MODEL slx_9b403d1e33a8
CONFIG AbsTol = auto
CONFIG EnableMultiTasking = off
CONFIG FixedStep = auto
CONFIG MaxStep = auto
CONFIG MinStep = auto
CONFIG RelTol = 1e-3
CONFIG SampleTimeConstraint = Unconstrained
CONFIG Solver = VariableStepAuto
CONFIG SolverName = VariableStepAuto
CONFIG StartTime = 0.0
CONFIG StopTime = 10.0
BLOCK [SubSystem] CAD2_1
  Ports = [0, 0, 0, 0, 0, 1, 1]
  RequestExecContextInheritance = off
BLOCK [PMIOPort] CAD2_1/F
  Port = 2
  Side = Right
BLOCK [PMIOPort] CAD2_1/F1
  Side = Left
BLOCK [Reference] CAD2_1/ReferenceFrame  REF=sm_lib/Frames and
Transforms/Reference
Frame
  Ports = [0, 0, 0, 0, 0, 0, 1]
  SourceBlock = sm_lib/Frames and
Transforms/Reference
Frame
  SourceProductBaseCode = MS
  SourceType = Reference
Frame
BLOCK [Reference] CAD2_1/Solid  REF=sm_lib/Body Elements/File Solid
  Ports = [0, 0, 0, 0, 0, 0, 1]
  SourceBlock = sm_lib/Body Elements/File Solid
  SourceProductBaseCode = MS
  SourceType = File Solid
BLOCK [Reference] CAD2_1/Transform  REF=sm_lib/Frames and
Transforms/Rigid
Transform
  Ports = [0, 0, 0, 0, 0, 1, 1]
  SourceBlock = sm_lib/Frames and
Transforms/Rigid
Transform
  SourceProductBaseCode = MS
  SourceType = Rigid
Transform
BLOCK [SubSystem] CAD2_2
  Ports = [0, 0, 0, 0, 0, 1, 1]
  RequestExecContextInheritance = off
BLOCK [PMIOPort] CAD2_2/F
  Side = Left
BLOCK [PMIOPort] CAD2_2/F1
  Port = 2
  Side = Right
BLOCK [Reference] CAD2_2/ReferenceFrame  REF=sm_lib/Frames and
Transforms/Reference
Frame
  Ports = [0, 0, 0, 0, 0, 0, 1]
  SourceBlock = sm_lib/Frames and
Transforms/Reference
Frame
  SourceProductBaseCode = MS
  SourceType = Reference
Frame
BLOCK [Reference] CAD2_2/Solid  REF=sm_lib/Body Elements/File Solid
  Ports = [0, 0, 0, 0, 0, 0, 1]
  SourceBlock = sm_lib/Body Elements/File Solid
  SourceProductBaseCode = MS
  SourceType = File Solid
BLOCK [Reference] CAD2_2/Transform  REF=sm_lib/Frames and
Transforms/Rigid
Transform
  Ports = [0, 0, 0, 0, 0, 1, 1]
  SourceBlock = sm_lib/Frames and
Transforms/Rigid
Transform
  SourceProductBaseCode = MS
  SourceType = Rigid
Transform
BLOCK [Reference] CAD2_2/Transform1  REF=sm_lib/Frames and
Transforms/Rigid
Transform
  Ports = [0, 0, 0, 0, 0, 1, 1]
  SourceBlock = sm_lib/Frames and
Transforms/Rigid
Transform
  SourceProductBaseCode = MS
  SourceType = Rigid
Transform
BLOCK [SubSystem] CAD2_3
  Ports = [0, 0, 0, 0, 0, 1, 1]
  RequestExecContextInheritance = off
BLOCK [PMIOPort] CAD2_3/F
  Port = 2
  Side = Right
BLOCK [PMIOPort] CAD2_3/F1
  Side = Left
BLOCK [Reference] CAD2_3/ReferenceFrame  REF=sm_lib/Frames and
Transforms/Reference
Frame
  Ports = [0, 0, 0, 0, 0, 0, 1]
  SourceBlock = sm_lib/Frames and
Transforms/Reference
Frame
  SourceProductBaseCode = MS
  SourceType = Reference
Frame
BLOCK [Reference] CAD2_3/Solid  REF=sm_lib/Body Elements/File Solid
  Ports = [0, 0, 0, 0, 0, 0, 1]
  SourceBlock = sm_lib/Body Elements/File Solid
  SourceProductBaseCode = MS
  SourceType = File Solid
BLOCK [Reference] CAD2_3/Transform  REF=sm_lib/Frames and
Transforms/Rigid
Transform
  Ports = [0, 0, 0, 0, 0, 1, 1]
  SourceBlock = sm_lib/Frames and
Transforms/Rigid
Transform
  SourceProductBaseCode = MS
  SourceType = Rigid
Transform
BLOCK [Reference] CAD2_3/Transform1  REF=sm_lib/Frames and
Transforms/Rigid
Transform
  Ports = [0, 0, 0, 0, 0, 1, 1]
  SourceBlock = sm_lib/Frames and
Transforms/Rigid
Transform
  SourceProductBaseCode = MS
  SourceType = Rigid
Transform
BLOCK [SubSystem] CAD_1
  Ports = [0, 0, 0, 0, 0, 2]
  RequestExecContextInheritance = off
BLOCK [PMIOPort] CAD_1/F
  Port = 2
  Side = Left
BLOCK [PMIOPort] CAD_1/F1
  Side = Left
BLOCK [Reference] CAD_1/ReferenceFrame  REF=sm_lib/Frames and
Transforms/Reference
Frame
  Ports = [0, 0, 0, 0, 0, 0, 1]
  SourceBlock = sm_lib/Frames and
Transforms/Reference
Frame
  SourceProductBaseCode = MS
  SourceType = Reference
Frame
BLOCK [Reference] CAD_1/Solid  REF=sm_lib/Body Elements/File Solid
  Ports = [0, 0, 0, 0, 0, 0, 1]
  SourceBlock = sm_lib/Body Elements/File Solid
  SourceProductBaseCode = MS
  SourceType = File Solid
BLOCK [Reference] CAD_1/Transform  REF=sm_lib/Frames and
Transforms/Rigid
Transform
  Ports = [0, 0, 0, 0, 0, 1, 1]
  SourceBlock = sm_lib/Frames and
Transforms/Rigid
Transform
  SourceProductBaseCode = MS
  SourceType = Rigid
Transform
BLOCK [Constant] Constant
  Value = 50
BLOCK [Reference] MechanismConfiguration  REF=sm_lib/Utilities/Mechanism
Configuration
  Ports = [0, 0, 0, 0, 0, 0, 1]
  SourceBlock = sm_lib/Utilities/Mechanism
Configuration
  SourceProductBaseCode = MS
  SourceType = Mechanism
Configuration
BLOCK [Reference] Prismatic  REF=sm_lib/Joints/Prismatic
Joint
  Ports = [0, 0, 0, 0, 0, 2, 1]
  SourceBlock = sm_lib/Joints/Prismatic
Joint
  SourceProductBaseCode = MS
  SourceType = Prismatic
Joint
BLOCK [Reference] Prismatic1  REF=sm_lib/Joints/Prismatic
Joint
  Ports = [0, 0, 0, 0, 0, 1, 1]
  SourceBlock = sm_lib/Joints/Prismatic
Joint
  SourceProductBaseCode = MS
  SourceType = Prismatic
Joint
BLOCK [Reference] Prismatic2  REF=sm_lib/Joints/Prismatic
Joint
  Ports = [0, 0, 0, 0, 0, 2, 1]
  SourceBlock = sm_lib/Joints/Prismatic
Joint
  SourceProductBaseCode = MS
  SourceType = Prismatic
Joint
BLOCK [Reference] Prismatic3  REF=sm_lib/Joints/Prismatic
Joint
  Ports = [0, 0, 0, 0, 0, 2, 1]
  SourceBlock = sm_lib/Joints/Prismatic
Joint
  SourceProductBaseCode = MS
  SourceType = Prismatic
Joint
BLOCK [Reference] Revolute  REF=sm_lib/Joints/Revolute Joint
  Ports = [0, 0, 0, 0, 0, 2, 1]
  SourceBlock = sm_lib/Joints/Revolute Joint
  SourceProductBaseCode = MS
  SourceType = Revolute Joint
BLOCK [Reference] Simulink-PS Converter1  REF=nesl_utility/Simulink-PS
Converter
  Ports = [1, 0, 0, 0, 0, 0, 1]
  SourceBlock = nesl_utility/Simulink-PS
Converter
  SourceProductBaseCode = SS
  SourceType = Simulink-PS
Converter
BLOCK [Reference] Simulink-PS Converter2  REF=nesl_utility/Simulink-PS
Converter
  Ports = [1, 0, 0, 0, 0, 0, 1]
  SourceBlock = nesl_utility/Simulink-PS
Converter
  SourceProductBaseCode = SS
  SourceType = Simulink-PS
Converter
BLOCK [Reference] Simulink-PS Converter3  REF=nesl_utility/Simulink-PS
Converter
  Ports = [1, 0, 0, 0, 0, 0, 1]
  SourceBlock = nesl_utility/Simulink-PS
Converter
  SourceProductBaseCode = SS
  SourceType = Simulink-PS
Converter
BLOCK [Reference] Simulink-PS Converter4  REF=nesl_utility/Simulink-PS
Converter
  Ports = [1, 0, 0, 0, 0, 0, 1]
  SourceBlock = nesl_utility/Simulink-PS
Converter
  SourceProductBaseCode = SS
  SourceType = Simulink-PS
Converter
BLOCK [Sin] Sine Wave1
  Amplitude = 0.1/3
  Phase = 180
  Ports = [0, 1]
  SampleTime = 0
BLOCK [Sin] Sine Wave2
  Amplitude = 0.01
  Ports = [0, 1]
  SampleTime = 0
BLOCK [Sin] Sine Wave3
  Amplitude = 0.1/3
  Ports = [0, 1]
  SampleTime = 0
BLOCK [Reference] Solver Configuration  REF=nesl_utility/Solver
Configuration
  Ports = [0, 0, 0, 0, 0, 0, 1]
  SourceBlock = nesl_utility/Solver
Configuration
  SourceProductBaseCode = SS
  SourceType = Solver
Configuration
BLOCK [Reference] Transform  REF=sm_lib/Frames and
Transforms/Rigid
Transform
  Ports = [0, 0, 0, 0, 0, 1, 1]
  SourceBlock = sm_lib/Frames and
Transforms/Rigid
Transform
  SourceProductBaseCode = MS
  SourceType = Rigid
Transform
BLOCK [Reference] Transform1  REF=sm_lib/Frames and
Transforms/Rigid
Transform
  Ports = [0, 0, 0, 0, 0, 1, 1]
  SourceBlock = sm_lib/Frames and
Transforms/Rigid
Transform
  SourceProductBaseCode = MS
  SourceType = Rigid
Transform
BLOCK [Reference] World  REF=sm_lib/Frames and
Transforms/World Frame
  Ports = [0, 0, 0, 0, 0, 0, 1]
  SourceBlock = sm_lib/Frames and
Transforms/World Frame
  SourceProductBaseCode = MS
  SourceType = World Frame
BLOCK [SubSystem] spindle2_1
  Ports = [0, 0, 0, 0, 0, 1]
  RequestExecContextInheritance = off
BLOCK [PMIOPort] spindle2_1/F
  Side = Left
BLOCK [Reference] spindle2_1/ReferenceFrame  REF=sm_lib/Frames and
Transforms/Reference
Frame
  Ports = [0, 0, 0, 0, 0, 0, 1]
  SourceBlock = sm_lib/Frames and
Transforms/Reference
Frame
  SourceProductBaseCode = MS
  SourceType = Reference
Frame
BLOCK [Reference] spindle2_1/Solid  REF=sm_lib/Body Elements/File Solid
  Ports = [0, 0, 0, 0, 0, 0, 1]
  SourceBlock = sm_lib/Body Elements/File Solid
  SourceProductBaseCode = MS
  SourceType = File Solid
BLOCK [Reference] spindle2_1/Transform  REF=sm_lib/Frames and
Transforms/Rigid
Transform
  Ports = [0, 0, 0, 0, 0, 1, 1]
  SourceBlock = sm_lib/Frames and
Transforms/Rigid
Transform
  SourceProductBaseCode = MS
  SourceType = Rigid
Transform
BLOCK [SubSystem] spindle_1
  Ports = [0, 0, 0, 0, 0, 1, 1]
  RequestExecContextInheritance = off
BLOCK [PMIOPort] spindle_1/F
  Port = 2
  Side = Right
BLOCK [PMIOPort] spindle_1/F1
  Side = Left
BLOCK [Reference] spindle_1/ReferenceFrame  REF=sm_lib/Frames and
Transforms/Reference
Frame
  Ports = [0, 0, 0, 0, 0, 0, 1]
  SourceBlock = sm_lib/Frames and
Transforms/Reference
Frame
  SourceProductBaseCode = MS
  SourceType = Reference
Frame
BLOCK [Reference] spindle_1/Solid  REF=sm_lib/Body Elements/File Solid
  Ports = [0, 0, 0, 0, 0, 0, 1]
  SourceBlock = sm_lib/Body Elements/File Solid
  SourceProductBaseCode = MS
  SourceType = File Solid
BLOCK [Reference] spindle_1/Transform  REF=sm_lib/Frames and
Transforms/Rigid
Transform
  Ports = [0, 0, 0, 0, 0, 1, 1]
  SourceBlock = sm_lib/Frames and
Transforms/Rigid
Transform
  SourceProductBaseCode = MS
  SourceType = Rigid
Transform
BLOCK [Reference] spindle_1/Transform1  REF=sm_lib/Frames and
Transforms/Rigid
Transform
  Ports = [0, 0, 0, 0, 0, 1, 1]
  SourceBlock = sm_lib/Frames and
Transforms/Rigid
Transform
  SourceProductBaseCode = MS
  SourceType = Rigid
Transform
BLOCK [SubSystem] table_1
  Ports = [0, 0, 0, 0, 0, 1, 1]
  RequestExecContextInheritance = off
BLOCK [PMIOPort] table_1/F
  Side = Left
BLOCK [PMIOPort] table_1/F1
  Port = 2
  Side = Right
BLOCK [Reference] table_1/ReferenceFrame  REF=sm_lib/Frames and
Transforms/Reference
Frame
  Ports = [0, 0, 0, 0, 0, 0, 1]
  SourceBlock = sm_lib/Frames and
Transforms/Reference
Frame
  SourceProductBaseCode = MS
  SourceType = Reference
Frame
BLOCK [Reference] table_1/Solid  REF=sm_lib/Body Elements/File Solid
  Ports = [0, 0, 0, 0, 0, 0, 1]
  SourceBlock = sm_lib/Body Elements/File Solid
  SourceProductBaseCode = MS
  SourceType = File Solid
BLOCK [Reference] table_1/Transform  REF=sm_lib/Frames and
Transforms/Rigid
Transform
  Ports = [0, 0, 0, 0, 0, 1, 1]
  SourceBlock = sm_lib/Frames and
Transforms/Rigid
Transform
  SourceProductBaseCode = MS
  SourceType = Rigid
Transform
BLOCK [Reference] table_1/Transform1  REF=sm_lib/Frames and
Transforms/Rigid
Transform
  Ports = [0, 0, 0, 0, 0, 1, 1]
  SourceBlock = sm_lib/Frames and
Transforms/Rigid
Transform
  SourceProductBaseCode = MS
  SourceType = Rigid
Transform
BLOCK [SubSystem] table_2
  Ports = [0, 0, 0, 0, 0, 1]
  RequestExecContextInheritance = off
BLOCK [Reference] table_2/Brick Solid  REF=sm_lib/Body Elements/Brick Solid
  NameLocation = top
  Ports = [0, 0, 0, 0, 0, 1]
  SourceBlock = sm_lib/Body Elements/Brick Solid
  SourceProductBaseCode = MS
  SourceType = Brick Solid
BLOCK [PMIOPort] table_2/F
  Side = Left
BLOCK [Reference] table_2/ReferenceFrame  REF=sm_lib/Frames and
Transforms/Reference
Frame
  Ports = [0, 0, 0, 0, 0, 0, 1]
  SourceBlock = sm_lib/Frames and
Transforms/Reference
Frame
  SourceProductBaseCode = MS
  SourceType = Reference
Frame
BLOCK [Reference] table_2/Rigid Transform  REF=sm_lib/Frames and
Transforms/Rigid
Transform
  Ports = [0, 0, 0, 0, 0, 1, 1]
  SourceBlock = sm_lib/Frames and
Transforms/Rigid
Transform
  SourceProductBaseCode = MS
  SourceType = Rigid
Transform
BLOCK [Reference] table_2/Solid  REF=sm_lib/Body Elements/File Solid
  Ports = [0, 0, 0, 0, 0, 1, 1]
  SourceBlock = sm_lib/Body Elements/File Solid
  SourceProductBaseCode = MS
  SourceType = File Solid
BLOCK [Reference] table_2/Transform  REF=sm_lib/Frames and
Transforms/Rigid
Transform
  Ports = [0, 0, 0, 0, 0, 1, 1]
  SourceBlock = sm_lib/Frames and
Transforms/Rigid
Transform
  SourceProductBaseCode = MS
  SourceType = Rigid
Transform
BLOCK [SubSystem] table_3
  Ports = [0, 0, 0, 0, 0, 2]
  RequestExecContextInheritance = off
BLOCK [PMIOPort] table_3/F
  Port = 2
  Side = Left
BLOCK [PMIOPort] table_3/F1
  Side = Left
BLOCK [Reference] table_3/ReferenceFrame  REF=sm_lib/Frames and
Transforms/Reference
Frame
  Ports = [0, 0, 0, 0, 0, 0, 1]
  SourceBlock = sm_lib/Frames and
Transforms/Reference
Frame
  SourceProductBaseCode = MS
  SourceType = Reference
Frame
BLOCK [Reference] table_3/Solid  REF=sm_lib/Body Elements/File Solid
  Ports = [0, 0, 0, 0, 0, 0, 1]
  SourceBlock = sm_lib/Body Elements/File Solid
  SourceProductBaseCode = MS
  SourceType = File Solid
BLOCK [Reference] table_3/Transform  REF=sm_lib/Frames and
Transforms/Rigid
Transform
  Ports = [0, 0, 0, 0, 0, 1, 1]
  SourceBlock = sm_lib/Frames and
Transforms/Rigid
Transform
  SourceProductBaseCode = MS
  SourceType = Rigid
Transform
BLOCK [Reference] table_3/Transform1  REF=sm_lib/Frames and
Transforms/Rigid
Transform
  Ports = [0, 0, 0, 0, 0, 1, 1]
  SourceBlock = sm_lib/Frames and
Transforms/Rigid
Transform
  SourceProductBaseCode = MS
  SourceType = Rigid
Transform
LINE CAD2_1/Transform:rconn -> CAD2_1/F:rconn
LINE CAD2_1:lconn -> Transform1:rconn
LINE CAD2_1:rconn -> Prismatic:lconn
LINE CAD2_2/Transform1:rconn -> CAD2_2/F1:rconn
LINE CAD2_2/Transform:rconn -> CAD2_2/F:rconn
LINE CAD2_2:lconn -> Prismatic1:rconn
LINE CAD2_2:rconn -> Prismatic2:lconn
LINE CAD2_3/Transform1:rconn -> CAD2_3/F1:rconn
LINE CAD2_3/Transform:rconn -> CAD2_3/F:rconn
LINE CAD2_3:lconn -> CAD_1:lconn
LINE CAD2_3:rconn -> Prismatic3:lconn
LINE CAD_1/Transform:rconn -> CAD_1/F:rconn
LINE CAD_1:lconn -> Transform:rconn
LINE Constant:1 -> Simulink-PS Converter4:1
LINE Prismatic1:lconn -> table_1:rconn
LINE Prismatic2:rconn -> table_2:lconn
LINE Prismatic3:rconn -> table_3:lconn
LINE Prismatic:rconn -> table_1:lconn
LINE Revolute:lconn -> spindle_1:rconn
LINE Revolute:rconn -> spindle2_1:lconn
LINE Simulink-PS Converter1:rconn -> Prismatic2:lconn
LINE Simulink-PS Converter2:rconn -> Prismatic3:lconn
LINE Simulink-PS Converter3:rconn -> Prismatic:lconn
LINE Simulink-PS Converter4:rconn -> Revolute:lconn
LINE Sine Wave1:1 -> Simulink-PS Converter1:1
LINE Sine Wave2:1 -> Simulink-PS Converter2:1
LINE Sine Wave3:1 -> Simulink-PS Converter3:1
LINE spindle2_1/Transform:rconn -> spindle2_1/F:rconn
LINE spindle_1/Transform1:rconn -> spindle_1/F1:rconn
LINE spindle_1/Transform:rconn -> spindle_1/F:rconn
LINE spindle_1:lconn -> table_3:lconn
LINE table_1/Transform1:rconn -> table_1/F1:rconn
LINE table_1/Transform:rconn -> table_1/F:rconn
LINE table_2/Brick Solid:lconn -> table_2/Rigid Transform:lconn
LINE table_2/Rigid Transform:rconn -> table_2/Solid:lconn
LINE table_2/Transform:rconn -> table_2/F:rconn
LINE table_3/Transform1:rconn -> table_3/F1:rconn
LINE table_3/Transform:rconn -> table_3/F:rconn
